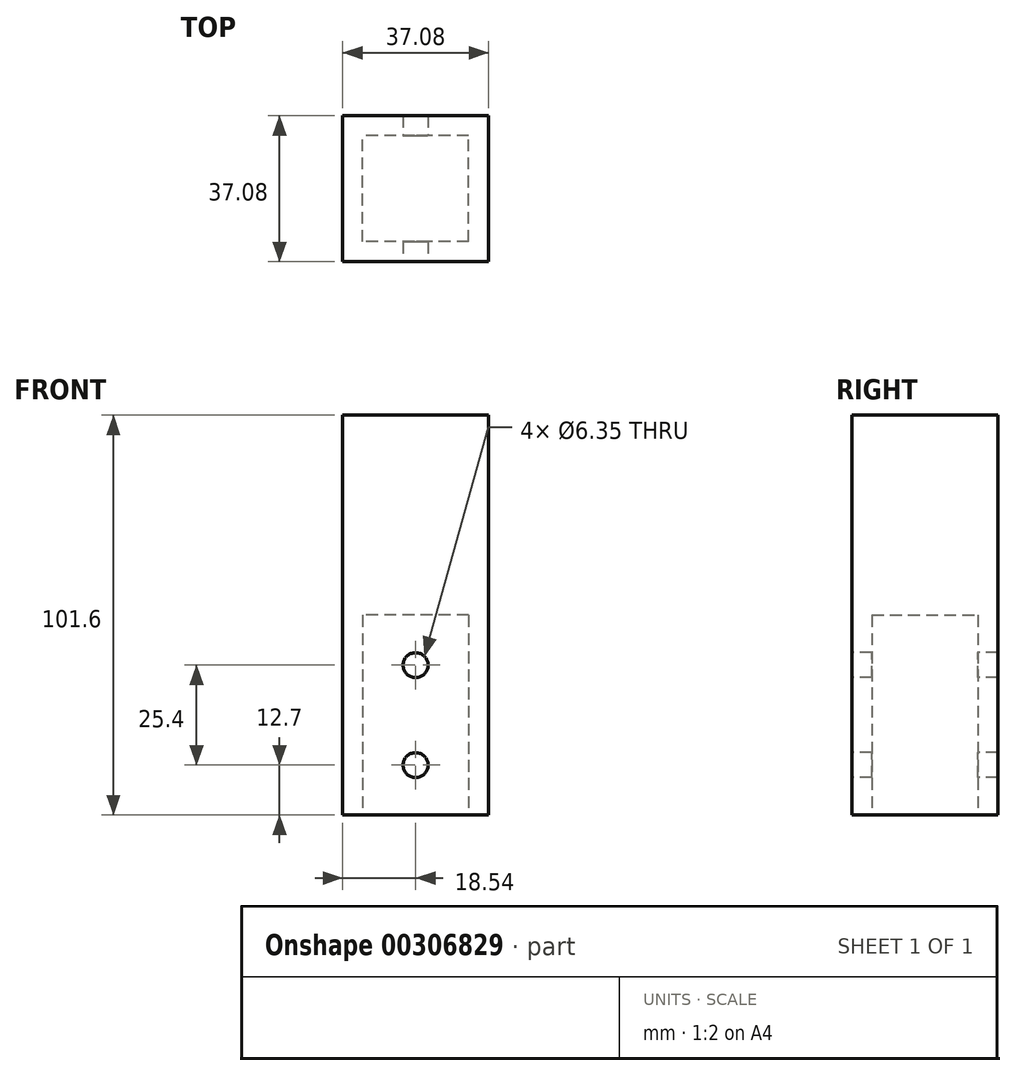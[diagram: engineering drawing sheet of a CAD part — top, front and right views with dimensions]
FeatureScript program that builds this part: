
annotation { "Feature Type Name" : "Feature", "Feature Type Description" : "" }
export const myFeature = defineFeature(function(context is Context, id is Id, definition is map)
    precondition{}
    {
        {
            var Q0;
            Q0=qCreatedBy(makeId("Top.planeOp"),FACE);
            var sketch = newSketch(context, id + "F0", { "sketchPlane" : qUnion([Q0])});
            skLineSegment(sketch, "E0.bottom", {"start": v(18.54, 18.54) * mm, "end": v(-18.54, 18.54) * mm});
            skLineSegment(sketch, "E0.top", {"start": v(18.54, -18.54) * mm, "end": v(-18.54, -18.54) * mm});
            skLineSegment(sketch, "E0.left", {"start": v(18.54, 18.54) * mm, "end": v(18.54, -18.54) * mm});
            skLineSegment(sketch, "E0.right", {"start": v(-18.54, 18.54) * mm, "end": v(-18.54, -18.54) * mm});
            skPoint(sketch, "E0.middle", {"position": v(0, 0) * mm});
            skSolve(sketch);
        }
        {
            var Q0;
            Q0=makeQuery(id+"F0.imprint","IMPRINT",FACE,{"disambiguationData":[TD([[makeQuery(id+"F0.imprint","IMPRINT",EDGE,{"derivedFrom":sQuery(id+"F0.wireOp",EDGE,"E0.bottom")}),1.0]])]});
            extrude(context, id + "F1", {"entities" : qUnion([Q0]), "depth" : 101.6 * mm});
        }
        {
            var Q0;
            Q0=makeQuery(id+"F1.opExtrude","CAP_FACE",FACE,{"disambiguationData":[OSD([sQuery(id+"F0.wireOp",EDGE,"E0.bottom"),sQuery(id+"F0.wireOp",EDGE,"E0.top"),sQuery(id+"F0.wireOp",EDGE,"E0.left"),sQuery(id+"F0.wireOp",EDGE,"E0.right")])],"isStart":true});
            var sketch = newSketch(context, id + "F2", { "sketchPlane" : qUnion([Q0])});
            skLineSegment(sketch, "E1.bottom", {"start": v(13.46, 13.46) * mm, "end": v(-13.46, 13.46) * mm});
            skLineSegment(sketch, "E1.top", {"start": v(13.46, -13.46) * mm, "end": v(-13.46, -13.46) * mm});
            skLineSegment(sketch, "E1.left", {"start": v(13.46, 13.46) * mm, "end": v(13.46, -13.46) * mm});
            skLineSegment(sketch, "E1.right", {"start": v(-13.46, 13.46) * mm, "end": v(-13.46, -13.46) * mm});
            skPoint(sketch, "E1.middle", {"position": v(0, 0) * mm});
            skSolve(sketch);
        }
        {
            var Q0;
            Q0=makeQuery(id+"F2.imprint","IMPRINT",FACE,{"disambiguationData":[TD([[makeQuery(id+"F2.imprint","IMPRINT",EDGE,{"derivedFrom":sQuery(id+"F2.wireOp",EDGE,"E1.bottom")}),1.0]])]});
            extrude(context, id + "F3", {"entities" : qUnion([Q0]), "operationType" : NewBodyOperationType.REMOVE, "oppositeDirection" : true, "depth" : 50.8 * mm});
        }
        {
            var Q0;
            Q0=makeQuery(id+"F1.opExtrude","SWEPT_FACE",FACE,{"disambiguationData":[OSD([sQuery(id+"F0.wireOp",EDGE,"E0.top")])]});
            var sketch = newSketch(context, id + "F4", { "sketchPlane" : qUnion([Q0])});
            skCircle(sketch, "E2", {"center": v(0, 12.7) * mm, "radius": 3.18 * mm});
            skSolve(sketch);
        }
        {
            var Q0;
            Q0=makeQuery(id+"F4.imprint","IMPRINT",FACE,{"disambiguationData":[TD([[makeQuery(id+"F4.imprint","IMPRINT",EDGE,{"derivedFrom":sQuery(id+"F4.wireOp",EDGE,"E2")}),1.0]])]});
            extrude(context, id + "F5", {"entities" : qUnion([Q0]), "operationType" : NewBodyOperationType.REMOVE, "endBound" : BoundingType.THROUGH_ALL, "oppositeDirection" : true, "depth" : 25.4 * mm});
        }
        {
            var Q0;
            Q0=makeQuery(id+"F1.opExtrude","SWEPT_FACE",FACE,{"disambiguationData":[OSD([sQuery(id+"F0.wireOp",EDGE,"E0.top")])]});
            var sketch = newSketch(context, id + "F6", { "sketchPlane" : qUnion([Q0])});
            skCircle(sketch, "E3", {"center": v(0, 38.1) * mm, "radius": 3.18 * mm});
            skSolve(sketch);
        }
        {
            var Q0;
            Q0=makeQuery(id+"F6.imprint","IMPRINT",FACE,{"disambiguationData":[TD([[makeQuery(id+"F6.imprint","IMPRINT",EDGE,{"derivedFrom":sQuery(id+"F6.wireOp",EDGE,"E3")}),1.0]])]});
            extrude(context, id + "F7", {"entities" : qUnion([Q0]), "operationType" : NewBodyOperationType.REMOVE, "endBound" : BoundingType.THROUGH_ALL, "oppositeDirection" : true, "depth" : 25.4 * mm});
        }
    });
